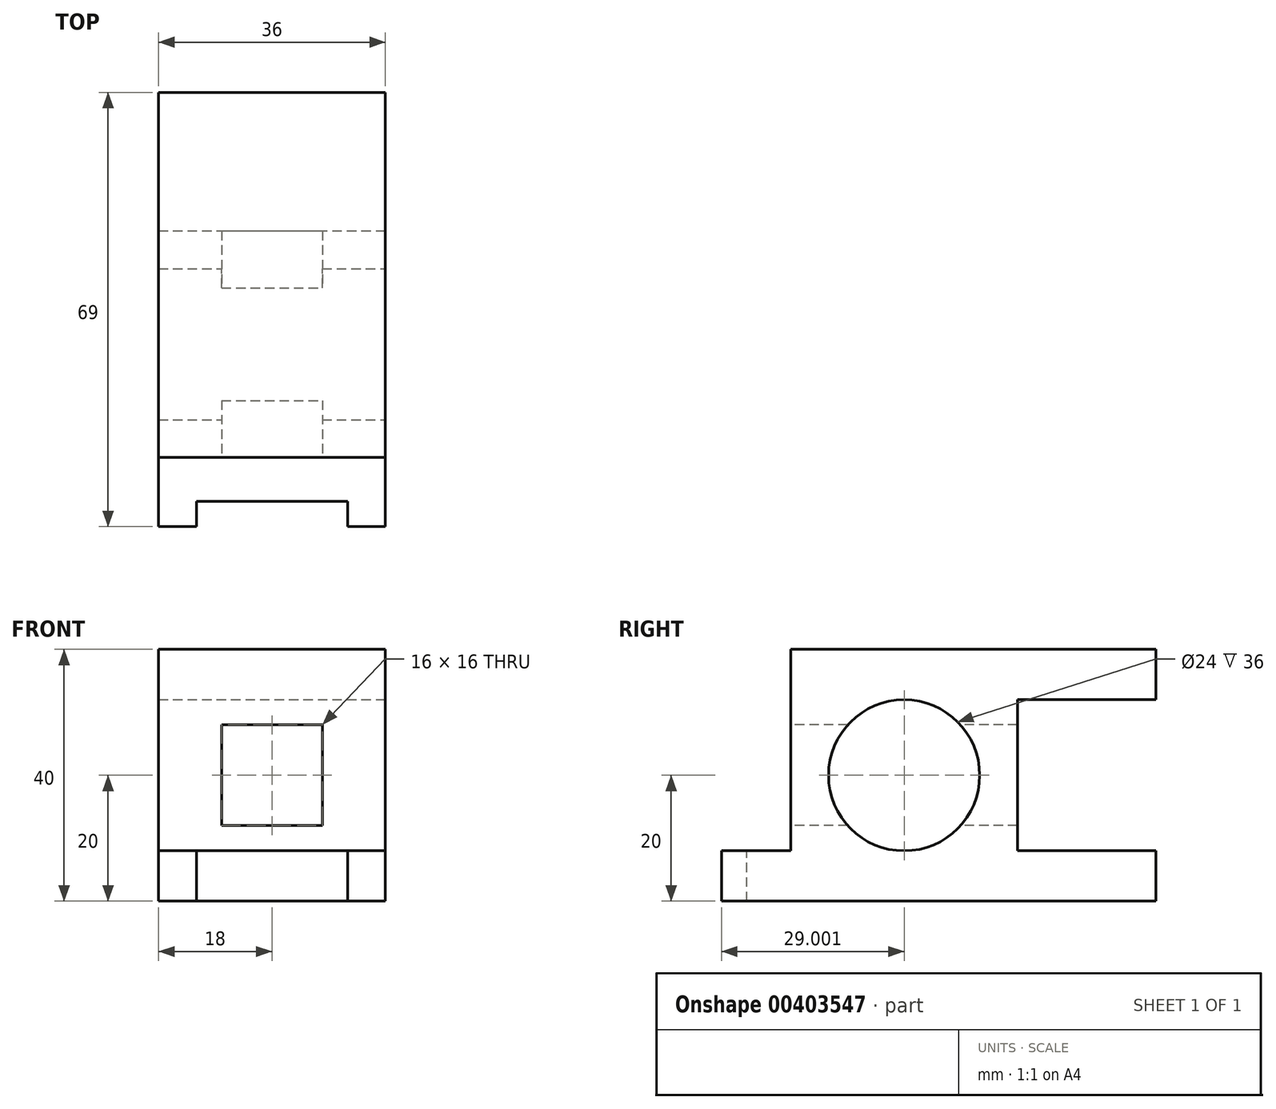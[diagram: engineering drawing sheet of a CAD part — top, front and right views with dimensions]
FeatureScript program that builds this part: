
annotation { "Feature Type Name" : "Feature", "Feature Type Description" : "" }
export const myFeature = defineFeature(function(context is Context, id is Id, definition is map)
    precondition{}
    {
        {
            var Q0;
            Q0=qCreatedBy(makeId("Right.planeOp"),FACE);
            var sketch = newSketch(context, id + "F0", { "sketchPlane" : qUnion([Q0])});
            skLineSegment(sketch, "E0.bottom", {"start": v(-40.24, 20) * mm, "end": v(28.76, 20) * mm});
            skLineSegment(sketch, "E0.top", {"start": v(-40.24, -20) * mm, "end": v(28.76, -20) * mm});
            skLineSegment(sketch, "E0.left", {"start": v(-40.24, 20) * mm, "end": v(-40.24, -20) * mm});
            skLineSegment(sketch, "E0.right", {"start": v(28.76, 20) * mm, "end": v(28.76, -20) * mm});
            skPoint(sketch, "E0.middle", {"position": v(-5.74, 0) * mm});
            skSolve(sketch);
        }
        {
            var Q0;
            Q0 = qSketchRegion(id + "F0", true);
            extrude(context, id + "F1", {"entities" : qUnion([Q0]), "endBound" : BoundingType.SYMMETRIC, "depth" : 36 * mm});
        }
        {
            var Q0;
            Q0=makeQuery(id+"F1.opExtrude","CAP_FACE",FACE,{"disambiguationData":[OSD([sQuery(id+"F0.wireOp",EDGE,"E0.bottom"),sQuery(id+"F0.wireOp",EDGE,"E0.top"),sQuery(id+"F0.wireOp",EDGE,"E0.left"),sQuery(id+"F0.wireOp",EDGE,"E0.right")])],"isStart":false});
            var sketch = newSketch(context, id + "F2", { "sketchPlane" : qUnion([Q0])});
            skLineSegment(sketch, "E1.bottom", {"start": v(-40.24, 20) * mm, "end": v(-29.24, 20) * mm});
            skLineSegment(sketch, "E1.top", {"start": v(-40.24, -12) * mm, "end": v(-29.24, -12) * mm});
            skLineSegment(sketch, "E1.left", {"start": v(-40.24, 20) * mm, "end": v(-40.24, -12) * mm});
            skLineSegment(sketch, "E1.right", {"start": v(-29.24, 20) * mm, "end": v(-29.24, -12) * mm});
            skSolve(sketch);
        }
        {
            var Q0;
            Q0 = qSketchRegion(id + "F2", true);
            extrude(context, id + "F3", {"entities" : qUnion([Q0]), "operationType" : NewBodyOperationType.REMOVE, "endBound" : BoundingType.THROUGH_ALL, "oppositeDirection" : true, "depth" : 25 * mm});
        }
        {
            var Q0;
            Q0=makeQuery(id+"F1.opExtrude","CAP_FACE",FACE,{"disambiguationData":[OSD([sQuery(id+"F0.wireOp",EDGE,"E0.bottom"),sQuery(id+"F0.wireOp",EDGE,"E0.top"),sQuery(id+"F0.wireOp",EDGE,"E0.left"),sQuery(id+"F0.wireOp",EDGE,"E0.right")])],"isStart":false});
            var sketch = newSketch(context, id + "F4", { "sketchPlane" : qUnion([Q0])});
            skLineSegment(sketch, "E2.bottom", {"start": v(28.76, 12) * mm, "end": v(6.76, 12) * mm});
            skLineSegment(sketch, "E2.top", {"start": v(28.76, -12) * mm, "end": v(6.76, -12) * mm});
            skLineSegment(sketch, "E2.left", {"start": v(28.76, 12) * mm, "end": v(28.76, -12) * mm});
            skLineSegment(sketch, "E2.right", {"start": v(6.76, 12) * mm, "end": v(6.76, -12) * mm});
            skSolve(sketch);
        }
        {
            var Q0;
            Q0 = qSketchRegion(id + "F4", true);
            extrude(context, id + "F5", {"entities" : qUnion([Q0]), "operationType" : NewBodyOperationType.REMOVE, "endBound" : BoundingType.THROUGH_ALL, "oppositeDirection" : true, "depth" : 25 * mm});
        }
        {
            var Q0;
            Q0=makeQuery(id+"F1.opExtrude","CAP_FACE",FACE,{"disambiguationData":[OSD([sQuery(id+"F0.wireOp",EDGE,"E0.bottom"),sQuery(id+"F0.wireOp",EDGE,"E0.top"),sQuery(id+"F0.wireOp",EDGE,"E0.left"),sQuery(id+"F0.wireOp",EDGE,"E0.right")])],"isStart":false});
            var sketch = newSketch(context, id + "F6", { "sketchPlane" : qUnion([Q0])});
            skCircle(sketch, "E3", {"center": v(-11.24, 0) * mm, "radius": 12 * mm});
            skSolve(sketch);
        }
        {
            var Q0;
            Q0 = qSketchRegion(id + "F6", true);
            extrude(context, id + "F7", {"entities" : qUnion([Q0]), "operationType" : NewBodyOperationType.REMOVE, "endBound" : BoundingType.THROUGH_ALL, "oppositeDirection" : true, "depth" : 25 * mm});
        }
        {
            var Q0;
            Q0=makeQuery(id+"F3.boolean.opBoolean","COPY",FACE,{"derivedFrom":makeQuery(id+"F3.opExtrude","SWEPT_FACE",FACE,{"disambiguationData":[OSD([sQuery(id+"F2.wireOp",EDGE,"E1.right")])]})});
            var sketch = newSketch(context, id + "F8", { "sketchPlane" : qUnion([Q0])});
            skLineSegment(sketch, "E4.bottom", {"start": v(-8, 8) * mm, "end": v(8, 8) * mm});
            skLineSegment(sketch, "E4.top", {"start": v(-8, -8) * mm, "end": v(8, -8) * mm});
            skLineSegment(sketch, "E4.left", {"start": v(-8, 8) * mm, "end": v(-8, -8) * mm});
            skLineSegment(sketch, "E4.right", {"start": v(8, 8) * mm, "end": v(8, -8) * mm});
            skSolve(sketch);
        }
        {
            var Q0;
            Q0 = qSketchRegion(id + "F8", true);
            extrude(context, id + "F9", {"entities" : qUnion([Q0]), "operationType" : NewBodyOperationType.REMOVE, "endBound" : BoundingType.THROUGH_ALL, "oppositeDirection" : true, "depth" : 25 * mm});
        }
        {
            var Q0;
            Q0=makeQuery(id+"F3.boolean.opBoolean","COPY",FACE,{"derivedFrom":makeQuery(id+"F3.opExtrude","SWEPT_FACE",FACE,{"disambiguationData":[OSD([sQuery(id+"F2.wireOp",EDGE,"E1.top")])]})});
            var sketch = newSketch(context, id + "F10", { "sketchPlane" : qUnion([Q0])});
            skLineSegment(sketch, "E5.bottom", {"start": v(-12, -40.24) * mm, "end": v(12, -40.24) * mm});
            skLineSegment(sketch, "E5.top", {"start": v(-12, -36.24) * mm, "end": v(12, -36.24) * mm});
            skLineSegment(sketch, "E5.left", {"start": v(-12, -40.24) * mm, "end": v(-12, -36.24) * mm});
            skLineSegment(sketch, "E5.right", {"start": v(12, -40.24) * mm, "end": v(12, -36.24) * mm});
            skSolve(sketch);
        }
        {
            var Q0;
            Q0 = qSketchRegion(id + "F10", true);
            extrude(context, id + "F11", {"entities" : qUnion([Q0]), "operationType" : NewBodyOperationType.REMOVE, "endBound" : BoundingType.THROUGH_ALL, "oppositeDirection" : true, "depth" : 25 * mm});
        }
    });
